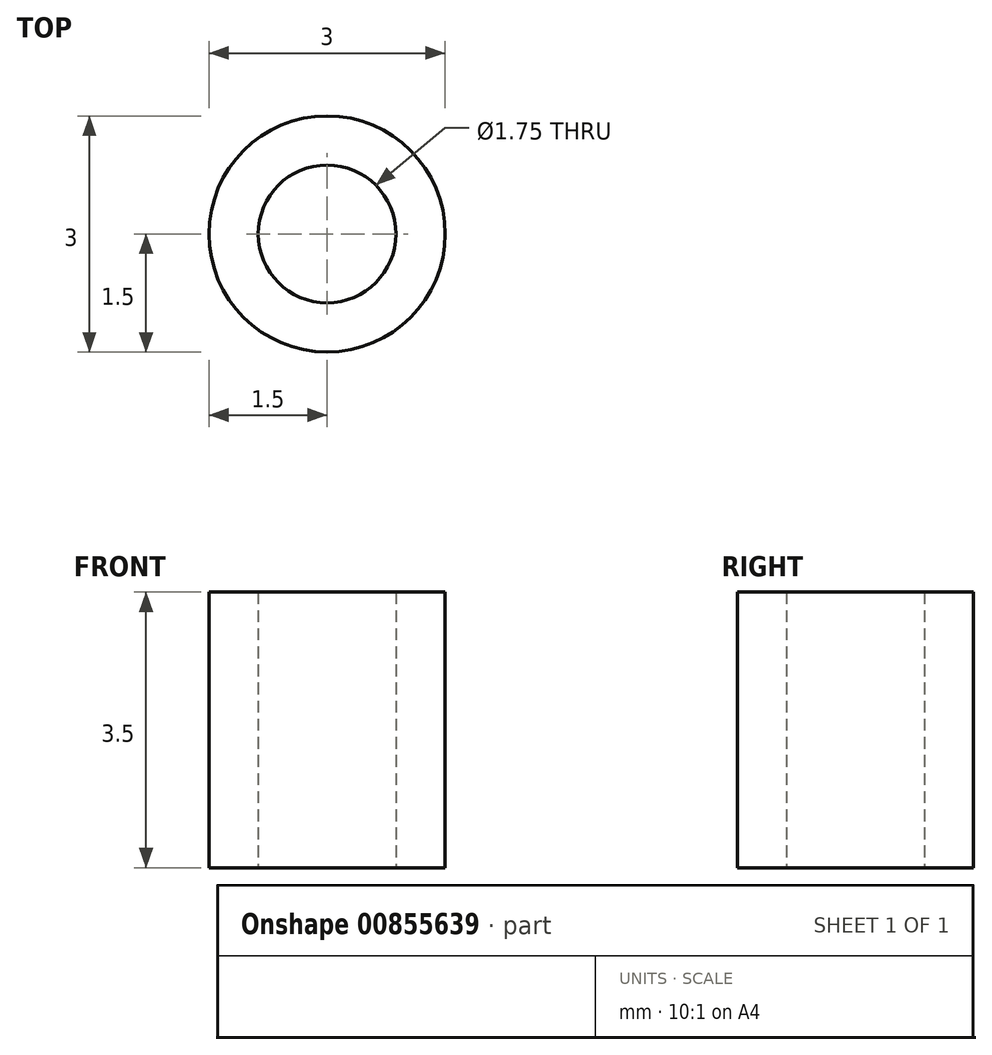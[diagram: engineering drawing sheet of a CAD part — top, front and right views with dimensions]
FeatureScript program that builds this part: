
annotation { "Feature Type Name" : "Feature", "Feature Type Description" : "" }
export const myFeature = defineFeature(function(context is Context, id is Id, definition is map)
    precondition{}
    {
        {
            var Q0;
            Q0=qCreatedBy(makeId("Top.planeOp"),FACE);
            var sketch = newSketch(context, id + "F0", { "sketchPlane" : qUnion([Q0])});
            skCircle(sketch, "E0", {"center": v(0, 0) * mm, "radius": 0.87 * mm});
            skCircle(sketch, "E1", {"center": v(0, 0) * mm, "radius": 1.5 * mm});
            skSolve(sketch);
        }
        {
            var Q0;
            Q0=makeQuery(id+"F0.imprint","IMPRINT",FACE,{"disambiguationData":[TD([[makeQuery(id+"F0.imprint","IMPRINT",EDGE,{"derivedFrom":sQuery(id+"F0.wireOp",EDGE,"E0")}),-1.0]])]});
            extrude(context, id + "F1", {"entities" : qUnion([Q0]), "depth" : 3.5 * mm, "offsetDistance" : 25 * mm});
        }
    });
